# Revit family: Clo_UK
name_source: partatom
category: Furniture
units: mm (PartAtom-declared; Revit-internal decimal feet)

## family parameters
Always vertical = Yes
Cut with Voids When Loaded = No
Enable Cutting in Views = Yes
Render Appearance Source = Family Geometry
Room Calculation Point = No
Shared = No
Work Plane-Based = No

## types (1)
- Club Chair
    Assembly Code = E2020200
    AssetType = Movable
    BIMObjectName = Clo : Club Chair
    Category = Pr_40_50_12_48 : Lounge chairs
    Color = Defined by Material Specified
    Default Elevation = 0 mm  [stored 0 ft]
    Description = Club Chair
    Export Type to IFC As = IfcFurnitureType
    FabricMaterial = TheSenatorGroup_Fabric_Camira_Blazer_CUZ3R_Stowe
    Finish = Fabric
    Height = 0 mm  [stored 0 ft]
    IfcExportAs = IfcFurnitureType
    IfcExportType = CHAIR
    IsBuiltIn = No
    Manufacturer = Allermuir
    ManufacturerAddress = Altham Business Park, Accrington , BB5 5YE , United Kingdom
    ManufacturerName = Allermuir
    ManufacturerPhone = +44 (0)1282 725000
    ManufacturerURL = https://www.allermuir.com
    Material = Moulded foam construction with plastic glides
    Model = CLW101
    ModelNumber = CLW101
    ModelReference = Club Chair
    Name = Lounge_Chair/CLW101_Club_Chair
    NominalDepth = 575 mm
    NominalHeight = 710 mm
    NominalLength = 610 mm  [stored 2.00131 ft]
    NominalWidth = 610 mm  [stored 2.00131 ft]
    OptionalFeatures = Fixed based with felt glides. Swivel auto-return with plastic glides. Multi-Fabrics.
    ProductInformation = https://www.allermuir.com
    SeatDepth = 490 mm  [stored 1.60761 ft]
    SeatWidth = 510 mm  [stored 1.67323 ft]
    SeatingHeight = 460 mm  [stored 1.50919 ft]
    SeatingType = Clo : Club Chair
    Shape = Circle
    Size = 610.0mm (W) x 575.0mm (D) x 710.0mm (H)
    Status = UNSET
    Style = Chair
    Type IFC Predefined Type = CHAIR
    URL = https://www.allermuir.com
    Uniclass2015Code = Pr_40_50_12_48
    Uniclass2015Title = Lounge chairs
    Uniclass2015Version = Products v1.41
    Version = 1
    WarrantyDescription = Allermuir warrant that its manufactured products are free from manufacturing defects - in materials or workmanship - for a period of ten (10) years. Allermuir will repair, or replace (at Allermuir's sole discretion) with comparable free of charge materials / components, any product / component which fails under normal use in a single shift environment, as a result of a defect in the materials and/ or workmanship.
    Weight = 17.5 kg

note: [stored X ft] marks values corroborated as IEEE doubles in the binary element streams (Revit-internal decimal feet)

## geometry (parser evidence)
native form markers: Sweep x4
no freeform markers — native parametric forms only
